# Revit family: 64432000
name_source: partatom
category: Plumbing Fixtures
revit_build: Autodesk Revit 2016 (Build: 20150714_1515(x64)
units: mm (PartAtom-declared; Revit-internal decimal feet)

## family parameters
Always vertical = Yes
Cut with Voids When Loaded = No
OmniClass Number = 23.45.55.00
OmniClass Title = Sanitary Faucets, Wastes
Part Type = Normal
Room Calculation Point = No
Round Connector Dimension = Use Diameter
Shared = No
Work Plane-Based = No

## types (1)
- 64432000 Washbasin faucet, 12 V
    2D/3D/BIM Files URL = http://static.hansa.com
    Advanced Features = Convertible for cold and premixed-water; Without draw-rod opening
    Aerator = Burglarproof
    Approval ACS = 15 ACC LY 337
    AssetType = Fixed
    BIMObjectName = 64432000
    Backflow Prevention EN1717 = EB
    BodyMaterial = Brass
    Brand = Hansa
    Catalog Drawing URL = http://static.hansa.com
    Category = Bathroom, public, health care
    Class = Touchless, separate transformer
    CloseOffRating = 0
    Color = Chrome
    Connection Size = G3/8
    ConvergoRefNr = 0087-1710-0041-DE
    Customs Code = 84818011
    DN Size = DN15
    Dimension Drawing URL = http://static.hansa.com
    DurationUnit = Year
    EAN Number = 4015474277090
    EMC Directive = 2004/108/EY
    EN Standard = EN 15091
    Electrical Connection = 12 VDC
    Electronic Parts = Infrared sensor; Solenoid valve; Separate power supply
    Extensions = No pop-up waste included
    FDV Document URL = http://www.hansa.com
    FaucetMainMaterial = Brass
    Features = Touchless, separate transformer
    Finish = Polished
    Flow Drawing URL = http://static.hansa.com
    Flow Rate At 300kPa With Flow Controller = 0.1 L/s
    FlowCoefficient = 0
    Group = Washbasin faucets
    Health Sales Arguments = Touch-free operation. Maximum comfort, maximum hygiene.
    IfcExportAs = IfcValveType
    IfcExportType = FAUCET
    InletConnectionSize = 10 mm  [stored 0.0328084 ft]
    Installation Type = Deck mounted
    Installation and Maintenance = http://static.hansa.com
    Intelligent After Flow Period = 2 s ± 1 s
    ManufacterURL = http://www.hansa.com
    Manufacturer = Hansa
    ManufacturerName = Hansa
    Market = AUT;BEL;CZE;DEU;ESP;FRA;INT;ITA;NLD;SVK
    Material = Brass
    Max Flow Period = 120.0 s
    Max. Hot Water Supply = 70 °C
    Mechanical Parts = Litter filter(s)
    Model = 64432000 Washbasin faucet, 12 V
    ModelReference = 64432000
    Mounting Holes = 1 mounting hole
    NBSDescription = Water supply fittings for wash basins and troughs
    NBSReference = 45-35-70/371
    Name = 64432000 Washbasin faucet, 12 V
    Name_en = 64432000 Washbasin faucet, 12 V
    NominalDepth = 167 mm  [stored 0.5479 ft]
    NominalHeight = 165 mm
    NominalWidth = 74 mm  [stored 0.242782 ft]
    Operating Voltage = 12 V
    Package Weight = 2.09 kg
    Package external Dimensions = 290 x 210 x 90
    Pipes = Flexible inlet pipes
    Product Code = 64432000
    Product Datasheet = http://www.hansa.com
    Product Family = HANSAELECTRA
    Product Image URL = http://static.hansa.com
    Product URL = http://static.hansa.com
    Projection = 112 mm
    Protection Class = IP 55 / transformer IP 40
    Recognition Range = Optimally preset
    Revision = 2
    Shape = Sculptured
    Size = 74x167x164.5 mm
    Spare Parts = http://static.hansa.com
    Spout Type = Fixed spout
    Temperature = Temperature fixable; Temperature regulator
    URL ACS = http://static.hansa.com
    Uniclass2 = Pr_40_30_96_99
    Uniclass2015Description = Washbasin thermostatic water supply sets
    Uniclass2015Reference = Pr_40_20_87_99
    Usage Group = Offices, personnel sanitary facilities; Pharmacies, Opticians, Dentists; Health centers & Child welfare clinics; Hospitals; Food stores; Gas stations; Schools
    Version = 2
    VersionDate = 01/01/2019
    WarrantyDescription = http://warranty.hansa.com
    WarrantyDurationUnit = Year
    WorkingPressure = 100 - 1000 kPa

note: [stored X ft] marks values corroborated as IEEE doubles in the binary element streams (Revit-internal decimal feet)

## geometry (parser evidence)
native form markers: Sweep x4
no freeform markers — native parametric forms only
